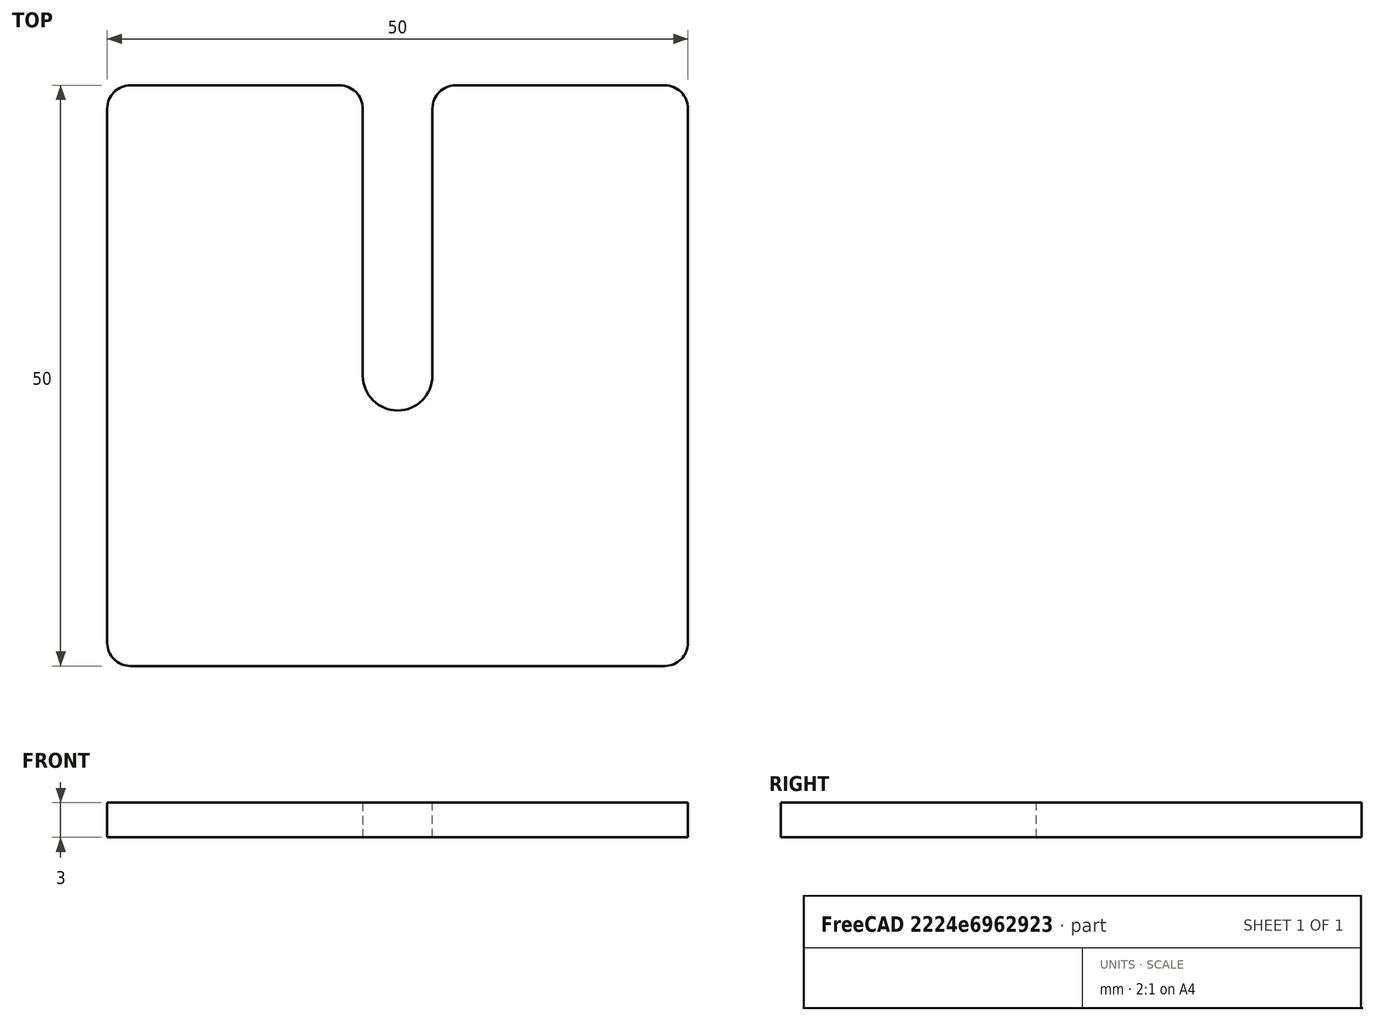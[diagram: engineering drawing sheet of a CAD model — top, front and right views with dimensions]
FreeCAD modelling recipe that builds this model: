
FCSTD DOCUMENT  (FreeCAD 0.18R14555 (Git shallow))
Label: spacer-3mm
License: All rights reserved
LicenseURL: http://en.wikipedia.org/wiki/All_rights_reserved
objects: Part::Box×2, Part::Cylinder×1, Part::MultiFuse×1, Part::Cut×1, Part::Fillet×1
note: 6 computed .brp shape members not serialized (recipe doc carries the construction recipe); baked Part::Feature solids carry a one-line shape summary decoded from their .brp

FEATURE [Part::Box] Box  label="Cube"
  AttacherType = Attacher::AttachEngine3D
  Height = 3
  Length = 50
  Placement = pos=(-25,-25,0) rot=(0,0,1;0rad)
  Width = 50
FEATURE [Part::Cylinder] Cylinder
  Angle = 360
  AttacherType = Attacher::AttachEngine3D
  Height = 10
  Radius = 3
FEATURE [Part::Box] Box001  label="Cube001"
  AttacherType = Attacher::AttachEngine3D
  Height = 10
  Length = 6
  Placement = pos=(-3,0,0) rot=(0,0,1;0rad)
  Width = 27
FEATURE [Part::MultiFuse] Fusion
  Shapes = -> [Box001,Cylinder]
FEATURE [Part::Cut] Cut
  Base = -> Box
  Tool = -> Fusion
FEATURE [Part::Fillet] Fillet
  Base = -> Cut
  Edges = 6 edges r=2: [Edge1,Edge3,Edge6,Edge15,Edge21,Edge24]
